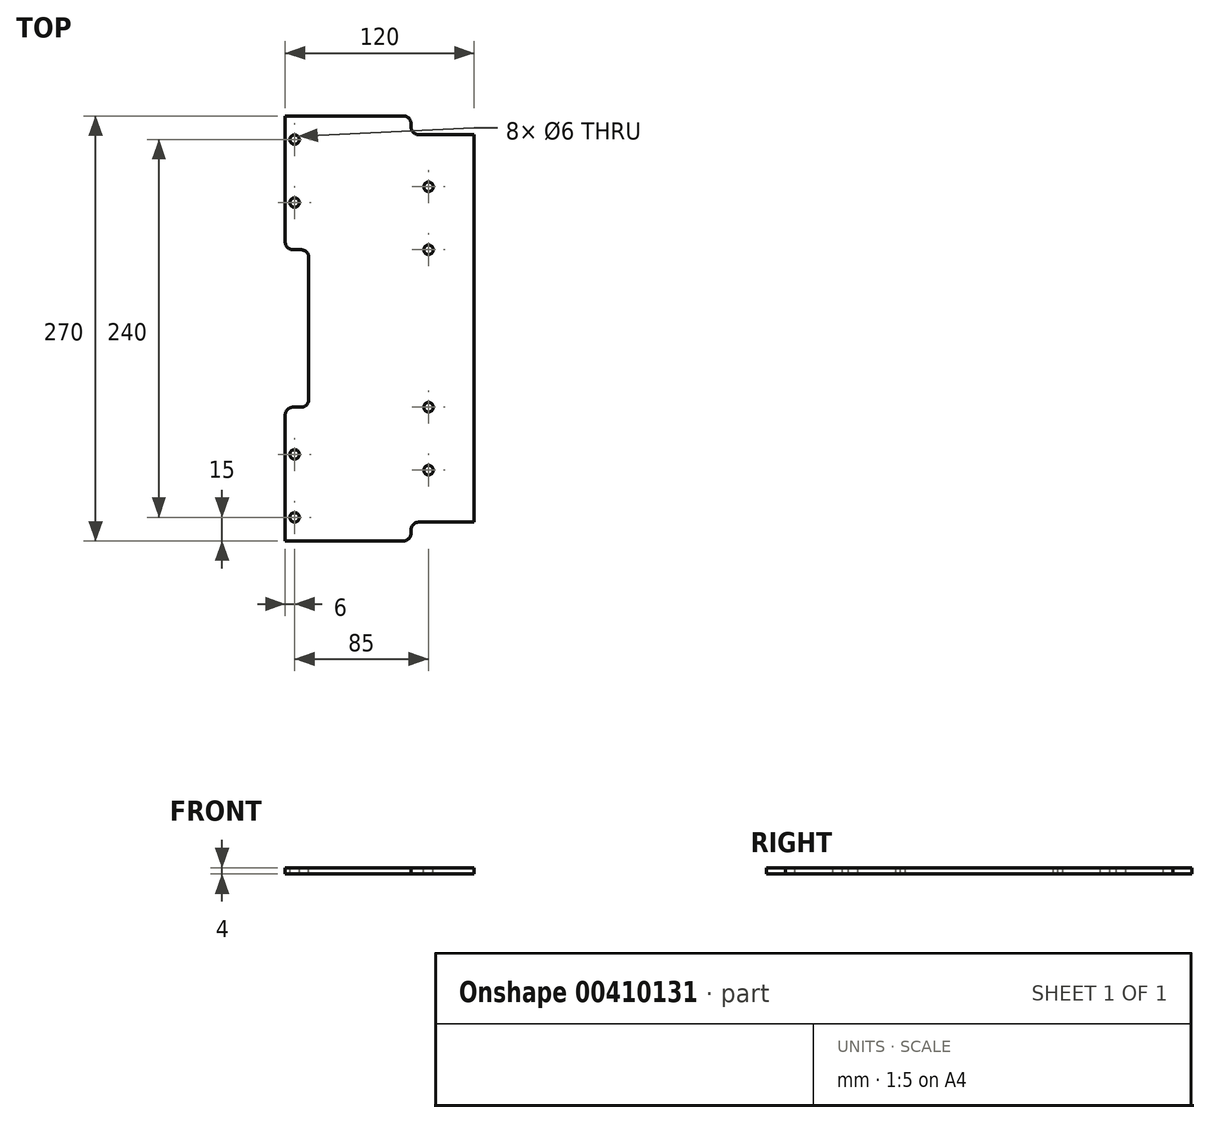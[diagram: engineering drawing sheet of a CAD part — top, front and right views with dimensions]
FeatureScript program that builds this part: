
annotation { "Feature Type Name" : "Feature", "Feature Type Description" : "" }
export const myFeature = defineFeature(function(context is Context, id is Id, definition is map)
    precondition{}
    {
        {
            var Q0;
            Q0=qCreatedBy(makeId("Top.planeOp"),FACE);
            var sketch = newSketch(context, id + "F0", { "sketchPlane" : qUnion([Q0])});
            skLineSegment(sketch, "E0.bottom", {"start": v(0, 0) * mm, "end": v(320, 0) * mm});
            skLineSegment(sketch, "E0.top", {"start": v(0, 420) * mm, "end": v(320, 420) * mm});
            skLineSegment(sketch, "E0.left", {"start": v(0, 0) * mm, "end": v(0, 420) * mm});
            skLineSegment(sketch, "E0.right", {"start": v(320, 0) * mm, "end": v(320, 420) * mm});
            skSolve(sketch);
        }
        {
            var Q0;
            Q0=qSketchRegion(id+"F0",true);
            extrude(context, id + "F1", {"entities" : qUnion([Q0]), "depth" : 4 * mm});
        }
        {
            var Q0;
            Q0=makeQuery(id+"F1.opExtrude","CAP_FACE",FACE,{"disambiguationData":[OSD([sQuery(id+"F0.wireOp",EDGE,"E0.bottom"),sQuery(id+"F0.wireOp",EDGE,"E0.top"),sQuery(id+"F0.wireOp",EDGE,"E0.left"),sQuery(id+"F0.wireOp",EDGE,"E0.right")])],"isStart":false});
            var sketch = newSketch(context, id + "F2", { "sketchPlane" : qUnion([Q0])});
            skLineSegment(sketch, "E1", {"start": v(290, 420) * mm, "end": v(320, 360) * mm});
            skLineSegment(sketch, "E2", {"start": v(290, 420) * mm, "end": v(320, 420) * mm});
            skLineSegment(sketch, "E3", {"start": v(320, 420) * mm, "end": v(320, 360) * mm});
            skLineSegment(sketch, "E4", {"start": v(290, 0) * mm, "end": v(320, 60) * mm});
            skLineSegment(sketch, "E5", {"start": v(290, 0) * mm, "end": v(320, 0) * mm});
            skLineSegment(sketch, "E6", {"start": v(320, 0) * mm, "end": v(320, 60) * mm});
            skLineSegment(sketch, "E7", {"start": v(0, 210) * mm, "end": v(320, 210) * mm, "construction": true});
            skLineSegment(sketch, "E8", {"start": v(163, 384) * mm, "end": v(163, 36) * mm, "construction": true});
            skPoint(sketch, "E9", {"position": v(163, 210) * mm});
            skLineSegment(sketch, "E10.bottom", {"start": v(213, 360) * mm, "end": v(113, 360) * mm});
            skLineSegment(sketch, "E10.top", {"start": v(213, 408) * mm, "end": v(113, 408) * mm});
            skLineSegment(sketch, "E10.left", {"start": v(218, 365) * mm, "end": v(218, 403) * mm});
            skLineSegment(sketch, "E10.right", {"start": v(108, 365) * mm, "end": v(108, 403) * mm});
            skPoint(sketch, "E10.middle", {"position": v(163, 384) * mm});
            skLineSegment(sketch, "E11.bottom", {"start": v(213, 12) * mm, "end": v(113, 12) * mm});
            skLineSegment(sketch, "E11.top", {"start": v(213, 60) * mm, "end": v(113, 60) * mm});
            skLineSegment(sketch, "E11.left", {"start": v(218, 17) * mm, "end": v(218, 55) * mm});
            skLineSegment(sketch, "E11.right", {"start": v(108, 17) * mm, "end": v(108, 55) * mm});
            skPoint(sketch, "E11.middle", {"position": v(163, 36) * mm});
            skPoint(sketch, "E12.visualSharp", {"position": v(108, 408) * mm});
            skArc(sketch, "E12.filletArc", {"start": v(113, 408) * mm, "mid": v(109.46, 406.54) * mm, "end": v(108, 403) * mm});
            skPoint(sketch, "E13.visualSharp", {"position": v(218, 408) * mm});
            skArc(sketch, "E13.filletArc", {"start": v(218, 403) * mm, "mid": v(216.54, 406.54) * mm, "end": v(213, 408) * mm});
            skPoint(sketch, "E14.visualSharp", {"position": v(108, 360) * mm});
            skArc(sketch, "E14.filletArc", {"start": v(108, 365) * mm, "mid": v(109.46, 361.46) * mm, "end": v(113, 360) * mm});
            skPoint(sketch, "E15.visualSharp", {"position": v(218, 360) * mm});
            skArc(sketch, "E15.filletArc", {"start": v(213, 360) * mm, "mid": v(216.54, 361.46) * mm, "end": v(218, 365) * mm});
            skPoint(sketch, "E16.visualSharp", {"position": v(218, 60) * mm});
            skArc(sketch, "E16.filletArc", {"start": v(218, 55) * mm, "mid": v(216.54, 58.54) * mm, "end": v(213, 60) * mm});
            skPoint(sketch, "E17.visualSharp", {"position": v(218, 12) * mm});
            skArc(sketch, "E17.filletArc", {"start": v(213, 12) * mm, "mid": v(216.54, 13.46) * mm, "end": v(218, 17) * mm});
            skPoint(sketch, "E18.visualSharp", {"position": v(108, 12) * mm});
            skArc(sketch, "E18.filletArc", {"start": v(108, 17) * mm, "mid": v(109.46, 13.46) * mm, "end": v(113, 12) * mm});
            skPoint(sketch, "E19.visualSharp", {"position": v(108, 60) * mm});
            skArc(sketch, "E19.filletArc", {"start": v(113, 60) * mm, "mid": v(109.46, 58.54) * mm, "end": v(108, 55) * mm});
            skLineSegment(sketch, "E20", {"start": v(0, 210) * mm, "end": v(50, 420) * mm});
            skLineSegment(sketch, "E21", {"start": v(0, 210) * mm, "end": v(50, 0) * mm});
            skLineSegment(sketch, "E22", {"start": v(50, 420) * mm, "end": v(0, 420) * mm});
            skLineSegment(sketch, "E23", {"start": v(0, 420) * mm, "end": v(0, 0) * mm});
            skLineSegment(sketch, "E24", {"start": v(0, 0) * mm, "end": v(50, 0) * mm});
            skSolve(sketch);
        }
        {
            var Q0;
            Q0=qSketchRegion(id+"F2",true);
            var Q1;
            Q1=makeQuery(id+"F1.opExtrude","CAP_FACE",FACE,{"disambiguationData":[OSD([sQuery(id+"F0.wireOp",EDGE,"E0.bottom"),sQuery(id+"F0.wireOp",EDGE,"E0.top"),sQuery(id+"F0.wireOp",EDGE,"E0.left"),sQuery(id+"F0.wireOp",EDGE,"E0.right")])],"isStart":true});
            extrude(context, id + "F3", {"entities" : qUnion([Q0]), "operationType" : NewBodyOperationType.REMOVE, "endBound" : BoundingType.UP_TO_SURFACE, "oppositeDirection" : true, "endBoundEntityFace" : qUnion([Q1]), "depth" : 25 * mm});
        }
        {
            var Q0;
            Q0=makeQuery(id+"F1.opExtrude","CAP_FACE",FACE,{"disambiguationData":[OSD([sQuery(id+"F0.wireOp",EDGE,"E0.bottom"),sQuery(id+"F0.wireOp",EDGE,"E0.top"),sQuery(id+"F0.wireOp",EDGE,"E0.left"),sQuery(id+"F0.wireOp",EDGE,"E0.right")])],"isStart":false});
            var sketch = newSketch(context, id + "F4", { "sketchPlane" : qUnion([Q0])});
            skLineSegment(sketch, "E25", {"start": v(67, 6) * mm, "end": v(277, 6) * mm, "construction": true});
            skCircle(sketch, "E26", {"center": v(67, 6) * mm, "radius": 3 * mm});
            skCircle(sketch, "E27.1.0.0", {"center": v(97, 6) * mm, "radius": 3 * mm});
            skCircle(sketch, "E27.2.0.0", {"center": v(127, 6) * mm, "radius": 3 * mm});
            skCircle(sketch, "E27.3.0.0", {"center": v(157, 6) * mm, "radius": 3 * mm});
            skCircle(sketch, "E27.4.0.0", {"center": v(187, 6) * mm, "radius": 3 * mm});
            skCircle(sketch, "E27.5.0.0", {"center": v(217, 6) * mm, "radius": 3 * mm});
            skCircle(sketch, "E27.6.0.0", {"center": v(247, 6) * mm, "radius": 3 * mm});
            skCircle(sketch, "E27.7.0.0", {"center": v(277, 6) * mm, "radius": 3 * mm});
            skLineSegment(sketch, "E27.direction1", {"start": v(67, 6) * mm, "end": v(97, 6) * mm, "construction": true});
            skLineSegment(sketch, "E28", {"start": v(70, 66) * mm, "end": v(310, 66) * mm, "construction": true});
            skCircle(sketch, "E29", {"center": v(64, 66) * mm, "radius": 3 * mm});
            skCircle(sketch, "E30.1.0.0", {"center": v(94, 66) * mm, "radius": 3 * mm});
            skCircle(sketch, "E30.2.0.0", {"center": v(124, 66) * mm, "radius": 3 * mm});
            skCircle(sketch, "E30.3.0.0", {"center": v(160, 66) * mm, "radius": 3 * mm, "construction": true});
            skCircle(sketch, "E30.4.0.0", {"center": v(190, 66) * mm, "radius": 3 * mm, "construction": true});
            skCircle(sketch, "E30.5.0.0", {"center": v(220, 66) * mm, "radius": 3 * mm});
            skCircle(sketch, "E30.6.0.0", {"center": v(250, 66) * mm, "radius": 3 * mm});
            skCircle(sketch, "E30.7.0.0", {"center": v(280, 66) * mm, "radius": 3 * mm});
            skCircle(sketch, "E30.8.0.0", {"center": v(310, 66) * mm, "radius": 3 * mm});
            skLineSegment(sketch, "E30.direction1", {"start": v(64, 66) * mm, "end": v(94, 66) * mm, "construction": true});
            skLineSegment(sketch, "E31", {"start": v(0, 210) * mm, "end": v(320, 210) * mm, "construction": true});
            skCircle(sketch, "E32.MirrorC", {"center": v(67, 414) * mm, "radius": 3 * mm});
            skCircle(sketch, "E33.MirrorC", {"center": v(64, 354) * mm, "radius": 3 * mm});
            skCircle(sketch, "E34.MirrorC", {"center": v(97, 414) * mm, "radius": 3 * mm});
            skCircle(sketch, "E35.MirrorC", {"center": v(310, 354) * mm, "radius": 3 * mm});
            skCircle(sketch, "E36.MirrorC", {"center": v(277, 414) * mm, "radius": 3 * mm});
            skCircle(sketch, "E37.MirrorC", {"center": v(94, 354) * mm, "radius": 3 * mm});
            skCircle(sketch, "E38.MirrorC", {"center": v(220, 354) * mm, "radius": 3 * mm});
            skLineSegment(sketch, "E39.MirrorCS", {"start": v(64, 354) * mm, "end": v(94, 354) * mm, "construction": true});
            skCircle(sketch, "E40.MirrorC", {"center": v(280, 354) * mm, "radius": 3 * mm});
            skCircle(sketch, "E41.MirrorC", {"center": v(124, 354) * mm, "radius": 3 * mm});
            skCircle(sketch, "E42.MirrorC", {"center": v(160, 354) * mm, "radius": 3 * mm, "construction": true});
            skCircle(sketch, "E43.MirrorC", {"center": v(190, 354) * mm, "radius": 3 * mm, "construction": true});
            skCircle(sketch, "E44.MirrorC", {"center": v(127, 414) * mm, "radius": 3 * mm});
            skCircle(sketch, "E45.MirrorC", {"center": v(250, 354) * mm, "radius": 3 * mm});
            skCircle(sketch, "E46.MirrorC", {"center": v(157, 414) * mm, "radius": 3 * mm});
            skCircle(sketch, "E47.MirrorC", {"center": v(187, 414) * mm, "radius": 3 * mm});
            skCircle(sketch, "E48.MirrorC", {"center": v(217, 414) * mm, "radius": 3 * mm});
            skCircle(sketch, "E49.MirrorC", {"center": v(247, 414) * mm, "radius": 3 * mm});
            skLineSegment(sketch, "E50.MirrorCS", {"start": v(67, 414) * mm, "end": v(277, 414) * mm, "construction": true});
            skLineSegment(sketch, "E51.MirrorCS", {"start": v(67, 414) * mm, "end": v(97, 414) * mm, "construction": true});
            skLineSegment(sketch, "E52.MirrorCS", {"start": v(70, 354) * mm, "end": v(310, 354) * mm, "construction": true});
            skSolve(sketch);
        }
        {
            var Q0;
            Q0=qSketchRegion(id+"F4",true);
            extrude(context, id + "F5", {"entities" : qUnion([Q0]), "operationType" : NewBodyOperationType.REMOVE, "oppositeDirection" : true, "depth" : 25 * mm});
        }
        {
            var Q0;
            Q0=makeQuery(id+"F1.opExtrude","CAP_FACE",FACE,{"disambiguationData":[OSD([sQuery(id+"F0.wireOp",EDGE,"E0.bottom"),sQuery(id+"F0.wireOp",EDGE,"E0.top"),sQuery(id+"F0.wireOp",EDGE,"E0.left"),sQuery(id+"F0.wireOp",EDGE,"E0.right")])],"isStart":false});
            var sketch = newSketch(context, id + "F6", { "sketchPlane" : qUnion([Q0])});
            skLineSegment(sketch, "E53", {"start": v(0, 210) * mm, "end": v(320, 210) * mm, "construction": true});
            skLineSegment(sketch, "E54", {"start": v(108, 365) * mm, "end": v(108, 55) * mm, "construction": true});
            skLineSegment(sketch, "E55", {"start": v(121, 90) * mm, "end": v(121, 330.2) * mm, "construction": true});
            skCircle(sketch, "E56", {"center": v(121, 90) * mm, "radius": 3 * mm});
            skCircle(sketch, "E57.0.1.0", {"center": v(121, 130) * mm, "radius": 3 * mm});
            skCircle(sketch, "E57.0.2.0", {"center": v(121, 170) * mm, "radius": 3 * mm});
            skCircle(sketch, "E57.1.0.0", {"center": v(206, 90) * mm, "radius": 3 * mm});
            skCircle(sketch, "E57.1.1.0", {"center": v(206, 130) * mm, "radius": 3 * mm});
            skCircle(sketch, "E57.1.2.0", {"center": v(206, 170) * mm, "radius": 3 * mm});
            skCircle(sketch, "E57.2.0.0", {"center": v(291, 80) * mm, "radius": 3 * mm});
            skCircle(sketch, "E57.2.1.0", {"center": v(291, 120) * mm, "radius": 3 * mm});
            skCircle(sketch, "E57.2.2.0", {"center": v(291, 160) * mm, "radius": 3 * mm});
            skLineSegment(sketch, "E57.direction1", {"start": v(121, 90) * mm, "end": v(206, 90) * mm, "construction": true});
            skLineSegment(sketch, "E57.direction2", {"start": v(121, 90) * mm, "end": v(121, 130) * mm, "construction": true});
            skCircle(sketch, "E58.MirrorC", {"center": v(121, 330) * mm, "radius": 3 * mm});
            skCircle(sketch, "E59.MirrorC", {"center": v(121, 290) * mm, "radius": 3 * mm});
            skCircle(sketch, "E60.MirrorC", {"center": v(206, 330) * mm, "radius": 3 * mm});
            skCircle(sketch, "E61.MirrorC", {"center": v(206, 250) * mm, "radius": 3 * mm});
            skCircle(sketch, "E62.MirrorC", {"center": v(291, 340) * mm, "radius": 3 * mm});
            skCircle(sketch, "E63.MirrorC", {"center": v(121, 250) * mm, "radius": 3 * mm});
            skCircle(sketch, "E64.MirrorC", {"center": v(206, 290) * mm, "radius": 3 * mm});
            skCircle(sketch, "E65.MirrorC", {"center": v(291, 300) * mm, "radius": 3 * mm});
            skCircle(sketch, "E66.MirrorC", {"center": v(291, 260) * mm, "radius": 3 * mm});
            skLineSegment(sketch, "E67.MirrorCS", {"start": v(121, 330) * mm, "end": v(121, 290) * mm, "construction": true});
            skLineSegment(sketch, "E68.MirrorCS", {"start": v(121, 330) * mm, "end": v(206, 330) * mm, "construction": true});
            skSolve(sketch);
        }
        {
            var Q0;
            Q0=qSketchRegion(id+"F6",true);
            extrude(context, id + "F7", {"entities" : qUnion([Q0]), "operationType" : NewBodyOperationType.REMOVE, "oppositeDirection" : true, "depth" : 25 * mm});
        }
        {
            var Q0;
            Q0=makeQuery(id+"F1.opExtrude","CAP_FACE",FACE,{"disambiguationData":[OSD([sQuery(id+"F0.wireOp",EDGE,"E0.bottom"),sQuery(id+"F0.wireOp",EDGE,"E0.top"),sQuery(id+"F0.wireOp",EDGE,"E0.left"),sQuery(id+"F0.wireOp",EDGE,"E0.right")])],"isStart":false});
            var sketch = newSketch(context, id + "F8", { "sketchPlane" : qUnion([Q0])});
            skLineSegment(sketch, "E69", {"start": v(0, 210) * mm, "end": v(320, 210) * mm, "construction": true});
            skCircle(sketch, "E70", {"center": v(15, 210) * mm, "radius": 3 * mm});
            skCircle(sketch, "E71.1.0.0", {"center": v(45, 210) * mm, "radius": 3 * mm});
            skLineSegment(sketch, "E71.direction1", {"start": v(15, 210) * mm, "end": v(45, 210) * mm, "construction": true});
            skSolve(sketch);
        }
        {
            var Q0;
            Q0=qSketchRegion(id+"F8",true);
            extrude(context, id + "F9", {"entities" : qUnion([Q0]), "operationType" : NewBodyOperationType.REMOVE, "oppositeDirection" : true, "depth" : 25 * mm});
        }
        {
            var Q0;
            Q0=makeQuery(id+"F1.opExtrude","CAP_FACE",FACE,{"disambiguationData":[OSD([sQuery(id+"F0.wireOp",EDGE,"E0.bottom"),sQuery(id+"F0.wireOp",EDGE,"E0.top"),sQuery(id+"F0.wireOp",EDGE,"E0.left"),sQuery(id+"F0.wireOp",EDGE,"E0.right")])],"isStart":false});
            var sketch = newSketch(context, id + "F10", { "sketchPlane" : qUnion([Q0])});
            skLineSegment(sketch, "E72", {"start": v(0, 210) * mm, "end": v(320, 210) * mm, "construction": true});
            skLineSegment(sketch, "E73.right", {"start": v(87, 355) * mm, "end": v(87, 350) * mm});
            skLineSegment(sketch, "E74", {"start": v(0, 335) * mm, "end": v(47, 335) * mm});
            skLineSegment(sketch, "E75", {"start": v(52, 340) * mm, "end": v(52, 355) * mm});
            skLineSegment(sketch, "E76", {"start": v(57, 360) * mm, "end": v(82, 360) * mm});
            skLineSegment(sketch, "E77", {"start": v(280, 340) * mm, "end": v(280, 338) * mm});
            skLineSegment(sketch, "E78", {"start": v(285, 333) * mm, "end": v(320, 333) * mm});
            skLineSegment(sketch, "E79", {"start": v(320, 333) * mm, "end": v(320, 210) * mm});
            skPoint(sketch, "E80.visualSharp", {"position": v(52, 335) * mm});
            skArc(sketch, "E80.filletArc", {"start": v(47, 335) * mm, "mid": v(50.54, 336.46) * mm, "end": v(52, 340) * mm});
            skPoint(sketch, "E81.newPointA", {"position": v(52, 360) * mm});
            skPoint(sketch, "E81.newPointB", {"position": v(0, 360) * mm});
            skArc(sketch, "E81.filletArc", {"start": v(57, 360) * mm, "mid": v(53.46, 358.54) * mm, "end": v(52, 355) * mm});
            skPoint(sketch, "E82.visualSharp", {"position": v(87, 360) * mm});
            skArc(sketch, "E82.filletArc", {"start": v(87, 355) * mm, "mid": v(85.54, 358.54) * mm, "end": v(82, 360) * mm});
            skArc(sketch, "E83.filletArc", {"start": v(87, 350) * mm, "mid": v(88.46, 346.46) * mm, "end": v(92, 345) * mm});
            skPoint(sketch, "E84.newPointA", {"position": v(280, 345) * mm});
            skPoint(sketch, "E84.newPointB", {"position": v(320, 345) * mm});
            skArc(sketch, "E84.filletArc", {"start": v(280, 340) * mm, "mid": v(278.54, 343.54) * mm, "end": v(275, 345) * mm});
            skPoint(sketch, "E85.visualSharp", {"position": v(280, 333) * mm});
            skArc(sketch, "E85.filletArc", {"start": v(280, 338) * mm, "mid": v(281.46, 334.46) * mm, "end": v(285, 333) * mm});
            skLineSegment(sketch, "E86", {"start": v(0, 335) * mm, "end": v(0, 210) * mm});
            skLineSegment(sketch, "E87", {"start": v(92, 345) * mm, "end": v(275, 345) * mm});
            skArc(sketch, "E88.MirrorCS", {"start": v(47, 85) * mm, "mid": v(50.54, 83.54) * mm, "end": v(52, 80) * mm});
            skArc(sketch, "E89.MirrorCS", {"start": v(87, 70) * mm, "mid": v(88.46, 73.54) * mm, "end": v(92, 75) * mm});
            skArc(sketch, "E90.MirrorCS", {"start": v(57, 60) * mm, "mid": v(53.46, 61.46) * mm, "end": v(52, 65) * mm});
            skLineSegment(sketch, "E91.MirrorCS", {"start": v(87, 65) * mm, "end": v(87, 70) * mm});
            skArc(sketch, "E92.MirrorCS", {"start": v(87, 65) * mm, "mid": v(85.54, 61.46) * mm, "end": v(82, 60) * mm});
            skLineSegment(sketch, "E93.MirrorCS", {"start": v(280, 80) * mm, "end": v(280, 82) * mm});
            skArc(sketch, "E94.MirrorCS", {"start": v(280, 82) * mm, "mid": v(281.46, 85.54) * mm, "end": v(285, 87) * mm});
            skArc(sketch, "E95.MirrorCS", {"start": v(280, 80) * mm, "mid": v(278.54, 76.46) * mm, "end": v(275, 75) * mm});
            skLineSegment(sketch, "E96.MirrorCS", {"start": v(52, 80) * mm, "end": v(52, 65) * mm});
            skLineSegment(sketch, "E97.MirrorCS", {"start": v(57, 60) * mm, "end": v(82, 60) * mm});
            skPoint(sketch, "E98.MirrorP", {"position": v(320, 75) * mm});
            skLineSegment(sketch, "E99.MirrorCS", {"start": v(320, 87) * mm, "end": v(320, 210) * mm});
            skPoint(sketch, "E100.MirrorP", {"position": v(52, 60) * mm});
            skPoint(sketch, "E101.MirrorP", {"position": v(52, 85) * mm});
            skPoint(sketch, "E102.MirrorP", {"position": v(87, 60) * mm});
            skPoint(sketch, "E103.MirrorP", {"position": v(280, 87) * mm});
            skLineSegment(sketch, "E104.MirrorCS", {"start": v(92, 75) * mm, "end": v(275, 75) * mm});
            skPoint(sketch, "E105.MirrorP", {"position": v(0, 60) * mm});
            skLineSegment(sketch, "E106.MirrorCS", {"start": v(0, 85) * mm, "end": v(0, 210) * mm});
            skLineSegment(sketch, "E107.MirrorCS", {"start": v(285, 87) * mm, "end": v(320, 87) * mm});
            skPoint(sketch, "E108.MirrorP", {"position": v(280, 75) * mm});
            skLineSegment(sketch, "E109.MirrorCS", {"start": v(0, 85) * mm, "end": v(47, 85) * mm});
            skSolve(sketch);
        }
        {
            var Q0;
            Q0=qSketchRegion(id+"F10",true);
            extrude(context, id + "F11", {"entities" : qUnion([Q0]), "operationType" : NewBodyOperationType.INTERSECT, "oppositeDirection" : true, "depth" : 25 * mm});
        }
        {
            var Q0;
            Q0=makeQuery(id+"F1.opExtrude","CAP_FACE",FACE,{"disambiguationData":[OSD([sQuery(id+"F0.wireOp",EDGE,"E0.bottom"),sQuery(id+"F0.wireOp",EDGE,"E0.top"),sQuery(id+"F0.wireOp",EDGE,"E0.left"),sQuery(id+"F0.wireOp",EDGE,"E0.right")])],"isStart":false});
            var sketch = newSketch(context, id + "F12", { "sketchPlane" : qUnion([Q0])});
            skPoint(sketch, "E110.oppositeSnap0", {"position": v(200, 345) * mm});
            skLineSegment(sketch, "E110.bottom", {"start": v(320, 345) * mm, "end": v(200, 345) * mm});
            skLineSegment(sketch, "E110.top", {"start": v(320, 75) * mm, "end": v(200, 75) * mm});
            skLineSegment(sketch, "E110.left", {"start": v(320, 345) * mm, "end": v(320, 75) * mm});
            skLineSegment(sketch, "E111", {"start": v(0, 210) * mm, "end": v(320, 210) * mm, "construction": true});
            skLineSegment(sketch, "E112.bottom", {"start": v(210, 160) * mm, "end": v(205, 160) * mm});
            skLineSegment(sketch, "E112.top", {"start": v(210, 260) * mm, "end": v(205, 260) * mm});
            skLineSegment(sketch, "E112.left", {"start": v(215, 165) * mm, "end": v(215, 255) * mm});
            skPoint(sketch, "E112.middle", {"position": v(200, 210) * mm});
            skPoint(sketch, "E113.orphan", {"position": v(185, 260) * mm});
            skPoint(sketch, "E114.orphan", {"position": v(185, 160) * mm});
            skLineSegment(sketch, "E115.trimOffspring", {"start": v(200, 155) * mm, "end": v(200, 75) * mm});
            skLineSegment(sketch, "E116", {"start": v(200, 345) * mm, "end": v(200, 265) * mm});
            skPoint(sketch, "E117", {"position": v(215, 210) * mm});
            skPoint(sketch, "E118.visualSharp", {"position": v(200, 260) * mm});
            skArc(sketch, "E118.filletArc", {"start": v(200, 265) * mm, "mid": v(201.46, 261.46) * mm, "end": v(205, 260) * mm});
            skPoint(sketch, "E119.visualSharp", {"position": v(215, 260) * mm});
            skArc(sketch, "E119.filletArc", {"start": v(215, 255) * mm, "mid": v(213.54, 258.54) * mm, "end": v(210, 260) * mm});
            skPoint(sketch, "E120.visualSharp", {"position": v(215, 160) * mm});
            skArc(sketch, "E120.filletArc", {"start": v(210, 160) * mm, "mid": v(213.54, 161.46) * mm, "end": v(215, 165) * mm});
            skPoint(sketch, "E121.visualSharp", {"position": v(200, 160) * mm});
            skArc(sketch, "E121.filletArc", {"start": v(205, 160) * mm, "mid": v(201.46, 158.54) * mm, "end": v(200, 155) * mm});
            skSolve(sketch);
        }
        {
            var Q0;
            Q0=qSketchRegion(id+"F12",true);
            extrude(context, id + "F13", {"entities" : qUnion([Q0]), "operationType" : NewBodyOperationType.INTERSECT, "oppositeDirection" : true, "depth" : 25 * mm});
        }
    });
